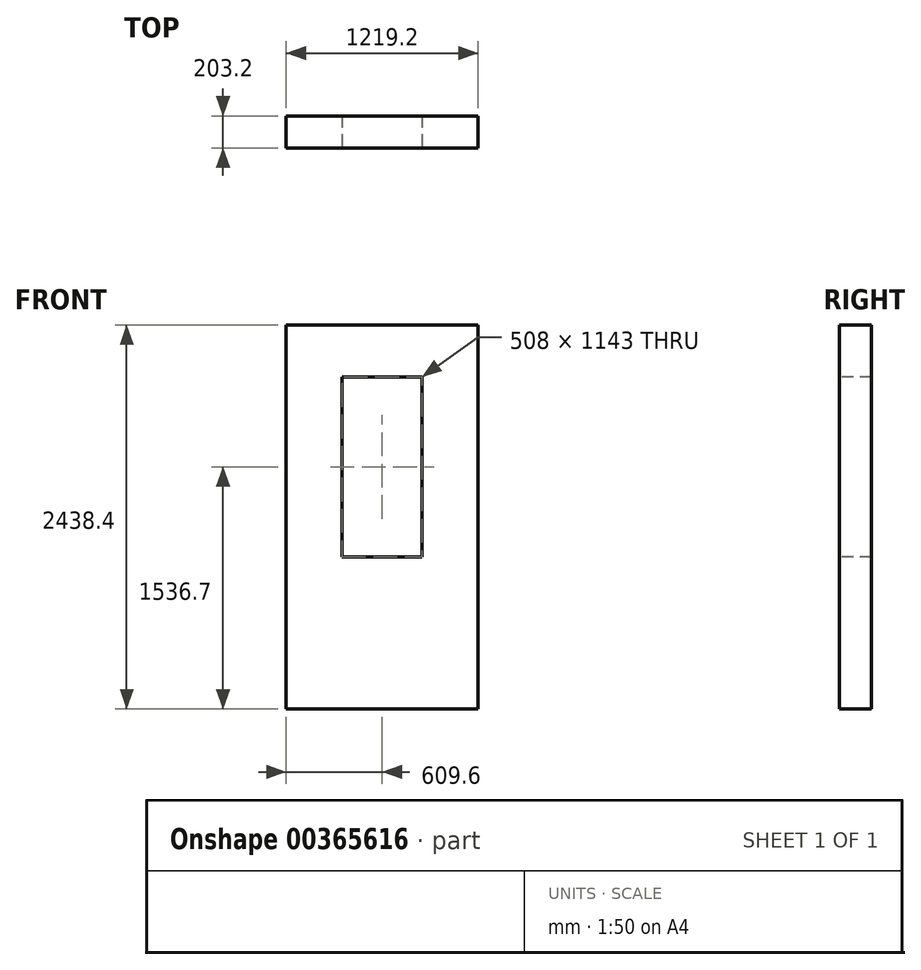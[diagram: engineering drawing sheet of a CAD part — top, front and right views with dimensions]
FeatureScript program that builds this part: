
annotation { "Feature Type Name" : "Feature", "Feature Type Description" : "" }
export const myFeature = defineFeature(function(context is Context, id is Id, definition is map)
    precondition{}
    {
        {
            var Q0;
            Q0=qCreatedBy(makeId("Front.planeOp"),FACE);
            var sketch = newSketch(context, id + "F0", { "sketchPlane" : qUnion([Q0])});
            skLineSegment(sketch, "E0.bottom", {"start": v(609.6, -1219.2) * mm, "end": v(-609.6, -1219.2) * mm});
            skLineSegment(sketch, "E0.top", {"start": v(609.6, 1219.2) * mm, "end": v(-609.6, 1219.2) * mm});
            skLineSegment(sketch, "E0.left", {"start": v(609.6, -1219.2) * mm, "end": v(609.6, 1219.2) * mm});
            skLineSegment(sketch, "E0.right", {"start": v(-609.6, -1219.2) * mm, "end": v(-609.6, 1219.2) * mm});
            skPoint(sketch, "E0.middle", {"position": v(0, 0) * mm});
            skSolve(sketch);
        }
        {
            var Q0;
            Q0 = qSketchRegion(id + "F0", true);
            extrude(context, id + "F1", {"entities" : qUnion([Q0]), "depth" : 203.2 * mm, "offsetDistance" : 25.4 * mm});
        }
        {
            var Q0;
            Q0=makeQuery(id+"F1.opExtrude","CAP_FACE",FACE,{"disambiguationData":[OSD([sQuery(id+"F0.wireOp",EDGE,"E0.bottom"),sQuery(id+"F0.wireOp",EDGE,"E0.top"),sQuery(id+"F0.wireOp",EDGE,"E0.left"),sQuery(id+"F0.wireOp",EDGE,"E0.right")])],"isStart":false});
            var sketch = newSketch(context, id + "F2", { "sketchPlane" : qUnion([Q0])});
            skLineSegment(sketch, "E1.bottom", {"start": v(254, 889) * mm, "end": v(-254, 889) * mm});
            skLineSegment(sketch, "E1.top", {"start": v(254, -254) * mm, "end": v(-254, -254) * mm});
            skLineSegment(sketch, "E1.left", {"start": v(254, 889) * mm, "end": v(254, -254) * mm});
            skLineSegment(sketch, "E1.right", {"start": v(-254, 889) * mm, "end": v(-254, -254) * mm});
            skPoint(sketch, "E1.middle", {"position": v(0, 317.5) * mm});
            skSolve(sketch);
        }
        {
            var Q0;
            Q0 = qSketchRegion(id + "F2", true);
            var Q1;
            Q1 = qConstructionFilter(qBodyType(qCreatedBy(id + "F2" ,EDGE), BodyType.WIRE), ConstructionObject.NO);
            extrude(context, id + "F3", {"entities" : qUnion([Q0]), "operationType" : NewBodyOperationType.REMOVE, "surfaceEntities" : qUnion([Q1]), "endBound" : BoundingType.THROUGH_ALL, "oppositeDirection" : true, "depth" : 25.4 * mm, "offsetDistance" : 25.4 * mm});
        }
    });
